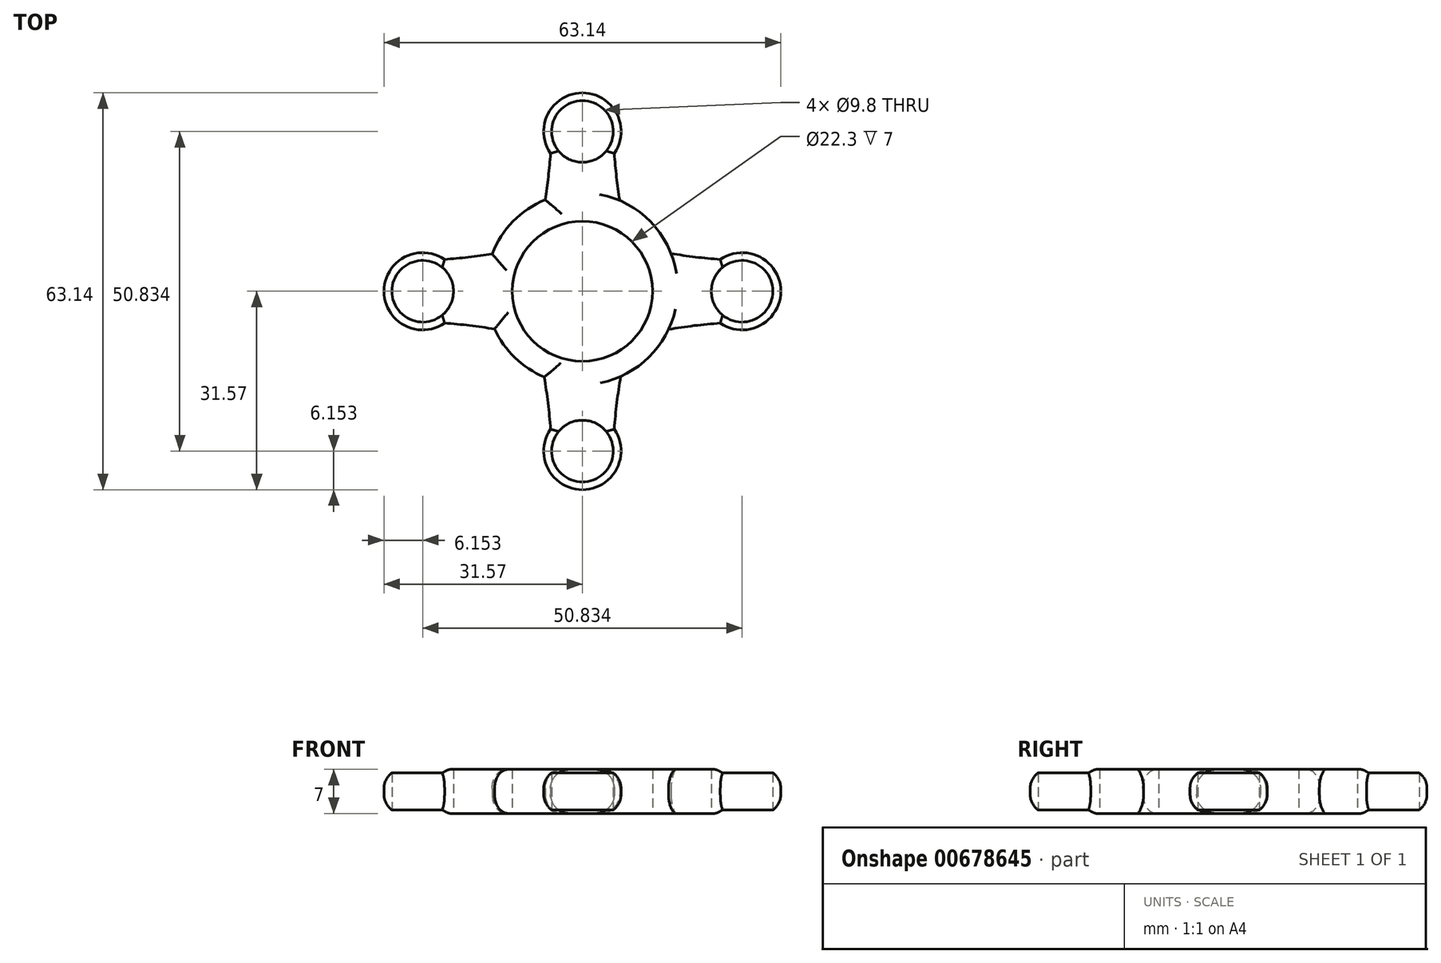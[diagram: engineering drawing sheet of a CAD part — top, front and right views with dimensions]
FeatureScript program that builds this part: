
annotation { "Feature Type Name" : "Feature", "Feature Type Description" : "" }
export const myFeature = defineFeature(function(context is Context, id is Id, definition is map)
    precondition{}
    {
        {
            var Q0;
            Q0=qCreatedBy(makeId("Top.planeOp"),FACE);
            var sketch = newSketch(context, id + "F0", { "sketchPlane" : qUnion([Q0])});
            skCircle(sketch, "E0", {"center": v(0, 0) * mm, "radius": 11.15 * mm});
            skCircle(sketch, "E1", {"center": v(-25.42, 0) * mm, "radius": 4.9 * mm});
            skArc(sketch, "E2", {"start": v(-25.4, 4.9) * mm, "mid": v(-16.94, 5.58) * mm, "end": v(-8.58, 7.12) * mm});
            skArc(sketch, "E3.MirrorCS", {"start": v(-25.4, -4.9) * mm, "mid": v(-16.94, -5.58) * mm, "end": v(-8.58, -7.12) * mm});
            skCircle(sketch, "E4.MirrorC", {"center": v(25.42, 0) * mm, "radius": 4.9 * mm});
            skArc(sketch, "E5.MirrorCS", {"start": v(25.4, 4.9) * mm, "mid": v(16.94, 5.58) * mm, "end": v(8.58, 7.12) * mm});
            skArc(sketch, "E6.MirrorCS", {"start": v(25.4, -4.9) * mm, "mid": v(16.94, -5.58) * mm, "end": v(8.58, -7.12) * mm});
            skCircle(sketch, "E7", {"center": v(-0.13, 0.41) * mm, "radius": 15.27 * mm});
            skCircle(sketch, "E8", {"center": v(-25.42, 0) * mm, "radius": 6.15 * mm});
            skCircle(sketch, "E9.MirrorC", {"center": v(25.42, 0) * mm, "radius": 6.15 * mm});
            skArc(sketch, "E10.1.0", {"start": v(-4.9, 25.4) * mm, "mid": v(-5.58, 16.94) * mm, "end": v(-7.12, 8.58) * mm});
            skArc(sketch, "E10.1.1", {"start": v(4.9, 25.4) * mm, "mid": v(5.58, 16.94) * mm, "end": v(7.12, 8.58) * mm});
            skCircle(sketch, "E10.1.2", {"center": v(0, 25.42) * mm, "radius": 6.15 * mm});
            skCircle(sketch, "E10.1.3", {"center": v(0, 25.42) * mm, "radius": 4.9 * mm});
            skArc(sketch, "E10.3.0", {"start": v(4.9, -25.4) * mm, "mid": v(5.58, -16.94) * mm, "end": v(7.12, -8.58) * mm});
            skArc(sketch, "E10.3.1", {"start": v(-4.9, -25.4) * mm, "mid": v(-5.58, -16.94) * mm, "end": v(-7.12, -8.58) * mm});
            skCircle(sketch, "E10.3.2", {"center": v(0, -25.42) * mm, "radius": 6.15 * mm});
            skCircle(sketch, "E10.3.3", {"center": v(0, -25.42) * mm, "radius": 4.9 * mm});
            skSolve(sketch);
        }
        {
            var Q0;
            Q0 = qSketchRegion(id + "F0", true);
            extrude(context, id + "F1", {"entities" : qUnion([Q0]), "depth" : 7 * mm, "offsetDistance" : 25 * mm});
        }
        {
            var Q0;
            {var subQ0=sQuery(id+"F0.wireOp",EDGE,"E7");Q0=makeQuery(id+"F1.opExtrude","CAP_EDGE",EDGE,{"disambiguationData":[OSD([subQ0]),TDD([makeQuery(id+"F0.imprint","IMPRINT",EDGE,{"disambiguationData":[TD([[makeQuery(id+"F0.imprint","INTERSECT",VERTEX,{"derivedFrom":[sQuery(id+"F0.wireOp",EDGE,"E2"),subQ0]}),1.0]])],"derivedFrom":subQ0})])],"isStart":false});}
            var Q1;
            Q1=makeQuery(id+"F1.opExtrude","CAP_EDGE",EDGE,{"disambiguationData":[OSD([sQuery(id+"F0.wireOp",EDGE,"E2")])],"isStart":false});
            var Q2;
            Q2=makeQuery(id+"F1.opExtrude","CAP_EDGE",EDGE,{"disambiguationData":[OSD([sQuery(id+"F0.wireOp",EDGE,"E8")])],"isStart":false});
            var Q3;
            Q3=makeQuery(id+"F1.opExtrude","CAP_EDGE",EDGE,{"disambiguationData":[OSD([sQuery(id+"F0.wireOp",EDGE,"E3.MirrorCS")])],"isStart":false});
            var Q4;
            {var subQ0=sQuery(id+"F0.wireOp",EDGE,"E7");Q4=makeQuery(id+"F1.opExtrude","CAP_EDGE",EDGE,{"disambiguationData":[OSD([subQ0]),TDD([makeQuery(id+"F0.imprint","IMPRINT",EDGE,{"disambiguationData":[TD([[makeQuery(id+"F0.imprint","INTERSECT",VERTEX,{"derivedFrom":[sQuery(id+"F0.wireOp",EDGE,"E3.MirrorCS"),subQ0]}),-1.0]])],"derivedFrom":subQ0})])],"isStart":false});}
            var Q5;
            Q5=makeQuery(id+"F1.opExtrude","CAP_EDGE",EDGE,{"disambiguationData":[OSD([sQuery(id+"F0.wireOp",EDGE,"E6.MirrorCS")])],"isStart":false});
            var Q6;
            Q6=makeQuery(id+"F1.opExtrude","CAP_EDGE",EDGE,{"disambiguationData":[OSD([sQuery(id+"F0.wireOp",EDGE,"E9.MirrorC")])],"isStart":false});
            var Q7;
            Q7=makeQuery(id+"F1.opExtrude","CAP_EDGE",EDGE,{"disambiguationData":[OSD([sQuery(id+"F0.wireOp",EDGE,"E5.MirrorCS")])],"isStart":false});
            var Q8;
            {var subQ0=sQuery(id+"F0.wireOp",EDGE,"E7");Q8=makeQuery(id+"F1.opExtrude","CAP_EDGE",EDGE,{"disambiguationData":[OSD([subQ0]),TDD([makeQuery(id+"F0.imprint","IMPRINT",EDGE,{"disambiguationData":[TD([[makeQuery(id+"F0.imprint","INTERSECT",VERTEX,{"derivedFrom":[sQuery(id+"F0.wireOp",EDGE,"E3.MirrorCS"),subQ0]}),-1.0]])],"derivedFrom":subQ0})])],"isStart":true});}
            var Q9;
            Q9=makeQuery(id+"F1.opExtrude","CAP_EDGE",EDGE,{"disambiguationData":[OSD([sQuery(id+"F0.wireOp",EDGE,"E3.MirrorCS")])],"isStart":true});
            var Q10;
            Q10=makeQuery(id+"F1.opExtrude","CAP_EDGE",EDGE,{"disambiguationData":[OSD([sQuery(id+"F0.wireOp",EDGE,"E8")])],"isStart":true});
            var Q11;
            Q11=makeQuery(id+"F1.opExtrude","CAP_EDGE",EDGE,{"disambiguationData":[OSD([sQuery(id+"F0.wireOp",EDGE,"E2")])],"isStart":true});
            var Q12;
            {var subQ0=sQuery(id+"F0.wireOp",EDGE,"E7");Q12=makeQuery(id+"F1.opExtrude","CAP_EDGE",EDGE,{"disambiguationData":[OSD([subQ0]),TDD([makeQuery(id+"F0.imprint","IMPRINT",EDGE,{"disambiguationData":[TD([[makeQuery(id+"F0.imprint","INTERSECT",VERTEX,{"derivedFrom":[sQuery(id+"F0.wireOp",EDGE,"E2"),subQ0]}),1.0]])],"derivedFrom":subQ0})])],"isStart":true});}
            var Q13;
            Q13=makeQuery(id+"F1.opExtrude","CAP_EDGE",EDGE,{"disambiguationData":[OSD([sQuery(id+"F0.wireOp",EDGE,"E5.MirrorCS")])],"isStart":true});
            var Q14;
            Q14=makeQuery(id+"F1.opExtrude","CAP_EDGE",EDGE,{"disambiguationData":[OSD([sQuery(id+"F0.wireOp",EDGE,"E9.MirrorC")])],"isStart":true});
            var Q15;
            Q15=makeQuery(id+"F1.opExtrude","CAP_EDGE",EDGE,{"disambiguationData":[OSD([sQuery(id+"F0.wireOp",EDGE,"E6.MirrorCS")])],"isStart":true});
            var Q16;
            Q16=makeQuery(id+"F1.opExtrude","CAP_EDGE",EDGE,{"disambiguationData":[OSD([sQuery(id+"F0.wireOp",EDGE,"E10.1.1")])],"isStart":false});
            var Q17;
            Q17=makeQuery(id+"F1.opExtrude","CAP_EDGE",EDGE,{"disambiguationData":[OSD([sQuery(id+"F0.wireOp",EDGE,"E10.1.2")])],"isStart":false});
            var Q18;
            Q18=makeQuery(id+"F1.opExtrude","CAP_EDGE",EDGE,{"disambiguationData":[OSD([sQuery(id+"F0.wireOp",EDGE,"E10.1.0")])],"isStart":false});
            var Q19;
            Q19=makeQuery(id+"F1.opExtrude","CAP_EDGE",EDGE,{"disambiguationData":[OSD([sQuery(id+"F0.wireOp",EDGE,"E3.MirrorCS")])],"isStart":false});
            var Q20;
            Q20=makeQuery(id+"F1.opExtrude","CAP_EDGE",EDGE,{"disambiguationData":[OSD([sQuery(id+"F0.wireOp",EDGE,"E8")])],"isStart":false});
            var Q21;
            Q21=makeQuery(id+"F1.opExtrude","CAP_EDGE",EDGE,{"disambiguationData":[OSD([sQuery(id+"F0.wireOp",EDGE,"E10.3.0")])],"isStart":false});
            var Q22;
            Q22=makeQuery(id+"F1.opExtrude","CAP_EDGE",EDGE,{"disambiguationData":[OSD([sQuery(id+"F0.wireOp",EDGE,"E10.3.2")])],"isStart":false});
            var Q23;
            Q23=makeQuery(id+"F1.opExtrude","CAP_EDGE",EDGE,{"disambiguationData":[OSD([sQuery(id+"F0.wireOp",EDGE,"E10.3.0")])],"isStart":true});
            var Q24;
            Q24=makeQuery(id+"F1.opExtrude","CAP_EDGE",EDGE,{"disambiguationData":[OSD([sQuery(id+"F0.wireOp",EDGE,"E10.3.2")])],"isStart":true});
            var Q25;
            Q25=makeQuery(id+"F1.opExtrude","CAP_EDGE",EDGE,{"disambiguationData":[OSD([sQuery(id+"F0.wireOp",EDGE,"E10.1.1")])],"isStart":true});
            var Q26;
            Q26=makeQuery(id+"F1.opExtrude","CAP_EDGE",EDGE,{"disambiguationData":[OSD([sQuery(id+"F0.wireOp",EDGE,"E10.1.2")])],"isStart":true});
            var Q27;
            Q27=makeQuery(id+"F1.opExtrude","CAP_EDGE",EDGE,{"disambiguationData":[OSD([sQuery(id+"F0.wireOp",EDGE,"E10.3.1")])],"isStart":true});
            var Q28;
            Q28=makeQuery(id+"F1.opExtrude","CAP_EDGE",EDGE,{"disambiguationData":[OSD([sQuery(id+"F0.wireOp",EDGE,"E3.MirrorCS")])],"isStart":true});
            var Q29;
            Q29=makeQuery(id+"F1.opExtrude","CAP_EDGE",EDGE,{"disambiguationData":[OSD([sQuery(id+"F0.wireOp",EDGE,"E2")])],"isStart":true});
            var Q30;
            Q30=makeQuery(id+"F1.opExtrude","CAP_EDGE",EDGE,{"disambiguationData":[OSD([sQuery(id+"F0.wireOp",EDGE,"E8")])],"isStart":true});
            var Q31;
            Q31=makeQuery(id+"F1.opExtrude","CAP_EDGE",EDGE,{"disambiguationData":[OSD([sQuery(id+"F0.wireOp",EDGE,"E10.1.0")])],"isStart":true});
            var Q32;
            Q32=makeQuery(id+"F1.opExtrude","CAP_EDGE",EDGE,{"disambiguationData":[OSD([sQuery(id+"F0.wireOp",EDGE,"E2")])],"isStart":false});
            var Q33;
            Q33=makeQuery(id+"F1.opExtrude","CAP_EDGE",EDGE,{"disambiguationData":[OSD([sQuery(id+"F0.wireOp",EDGE,"E10.3.1")])],"isStart":false});
            fillet(context, id + "F2", {"entities" : qUnion([Q0, Q1, Q2, Q3, Q4, Q5, Q6, Q7, Q8, Q9, Q10, Q11, Q12, Q13, Q14, Q15, Q16, Q17, Q18, Q19, Q20, Q21, Q22, Q23, Q24, Q25, Q26, Q27, Q28, Q29, Q30, Q31, Q32, Q33]), "radius" : 3 * mm, "tangentPropagation" : true, "allowEdgeOverflow" : false});
        }
    });
